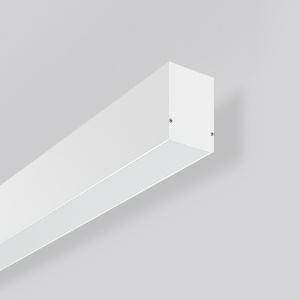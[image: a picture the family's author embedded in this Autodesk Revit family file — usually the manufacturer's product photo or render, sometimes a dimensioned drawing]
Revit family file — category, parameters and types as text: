
# Revit family: less_is_more_50_312609_002_1_80da
name_source: partatom
category: Lighting Fixtures
units: mm (PartAtom-declared; Revit-internal decimal feet)

## family parameters
Cut with Voids When Loaded = No
Host = Face
Light Source = No
Part Type = Normal
Room Calculation Point = No
Round Connector Dimension = Use Diameter
Shared = No

## types (1)
- LESS IS MORE 50 (1 x LED Modul 840, 1950 lm, 4000)
    Apparent Load = 15 VA
    CIE Flux Codes = 48 80 96 100 100
    Color Rendering = 80
    Color Temperature = 4000
    Default Elevation = 1800 mm
    Description = Series: LESS IS MORE 50
Linear wall luminaires. Housing: extruded aluminium profile, powder-coated. End cap aluminium powder-coated. Diffuser made of non-yellowing plastic (PMMA), opal. Direct light emission. Suitable for Wall (surface). LED unit with integrated converter interchangeable and removable. Suitable for through-wiring. With sensors or as a safety luminaire on request. 
Colour: traffic white, matt (RAL 9016)
Length: 1407 mm
Width: 67 mm
Height: 75 mm
Lamp: LED
Socket: without socket
Colour temperature: 4000K
Colour rendering index (CRI): 80
System power: 15 W
Rated luminous flux: 1950 lm
Luminous efficiency: 130 lm/W
Control gear: Regulated power supply
Protection class: I
Type of protection: IP 20
    Height = 75 mm
    Lamp = 1 x LED Modul 840
    Lamp Light Flux = 1950 lm
    Lamp count = 1
    Length = 1407 mm
    Lifetime = 50000 h
    Luminous efficacy = 130 lm/W
    Manufacturer = RZB
    ModVariant = No
    Model = 312609.002.1
    Mounting Place = Wall
    Mounting Type = Surface mounted
    Number of Poles = 1
    OnlyDefault = Yes
    Power Factor = 1
    Product Name = LESS IS MORE 50
    Product group = Surface mounted LED linear luminaires
    ProductGroupID = 2007
    Protection Class = Protection class I
    Protection Degree = IP 20
    RLX_Detail_Level = 1
    RLX_Emergency_Light_Flux = 0 lm
    RLX_Emergency_Type = 0
    RLX_Emergency_Type_DB = No
    RlxData = <blob elided: 35181 chars, md5=55793f08>
    Socket = socket
    Standby Power = 0 W
    System Light Flux = 1950 lm
    System Power = 15 W
    Type Comments = Product without accessories
    Type Image = 312606.002.jpg
    URL = http://relux.com
    VarID = ---
    Voltage = 0 V
    Weight = 0.00 kg
    Width = 67 mm

## geometry (parser evidence)
native form markers: Blend x4, Sweep x10
no freeform markers — native parametric forms only
